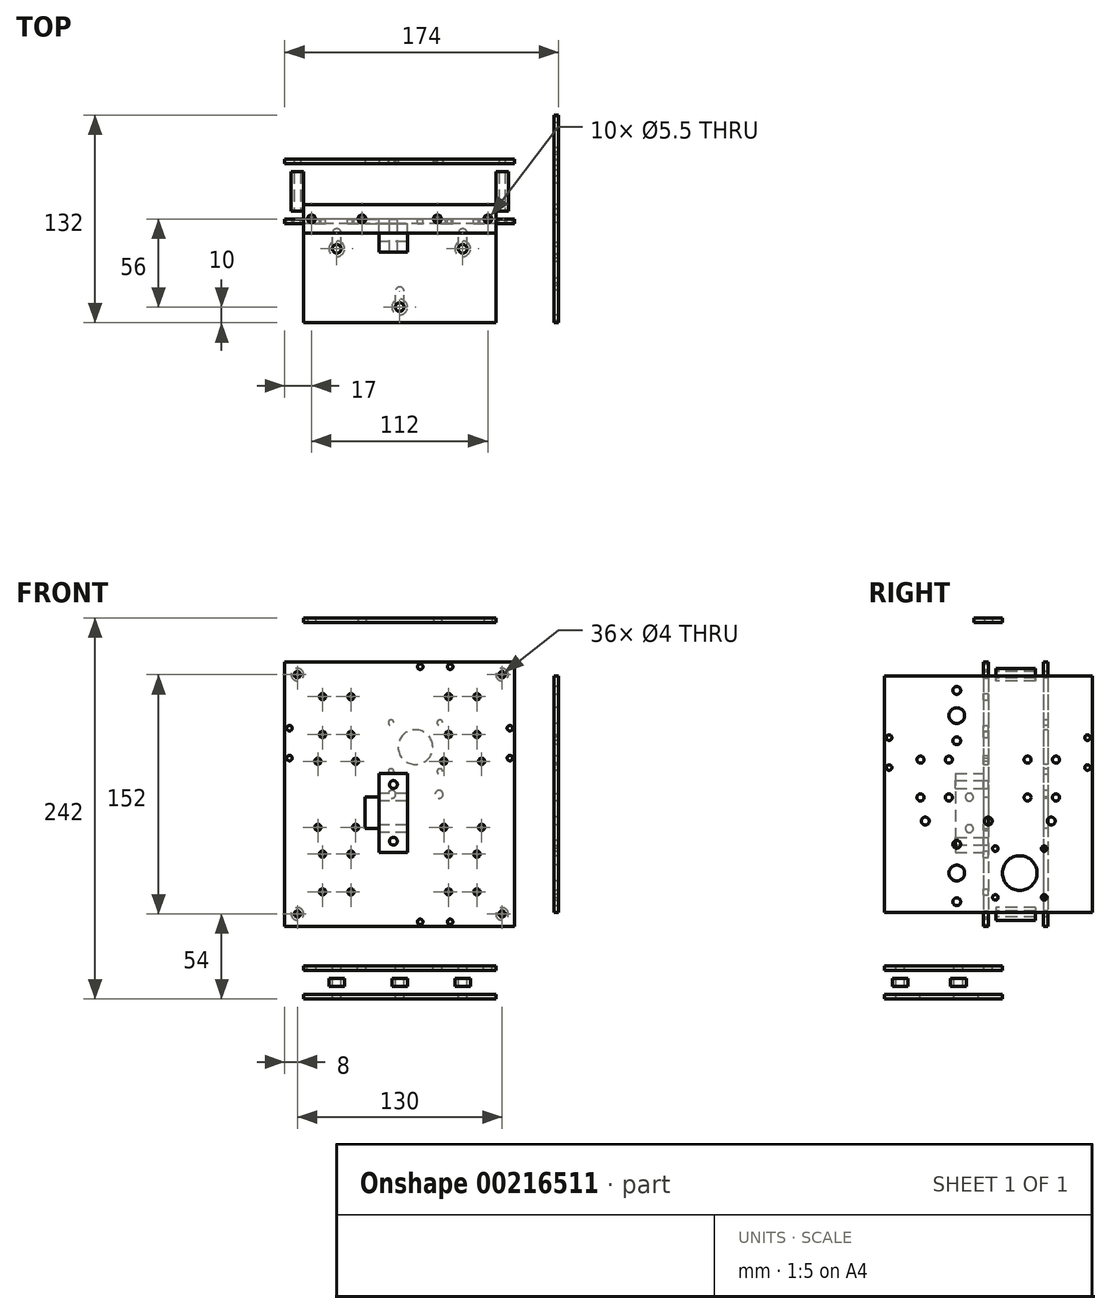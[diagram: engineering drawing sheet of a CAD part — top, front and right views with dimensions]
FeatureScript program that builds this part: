
annotation { "Feature Type Name" : "Feature", "Feature Type Description" : "" }
export const myFeature = defineFeature(function(context is Context, id is Id, definition is map)
    precondition{}
    {
        {
            assignVariable(context, id + "F0", {"name" : "Thickness", "anyValue" : 3});
        }
        {
            var Q0;
            Q0=qCreatedBy(makeId("Front.planeOp"),FACE);
            var sketch = newSketch(context, id + "F1", { "sketchPlane" : qUnion([Q0])});
            skLineSegment(sketch, "E0.bottom", {"start": v(73, 84) * mm, "end": v(-73, 84) * mm});
            skLineSegment(sketch, "E0.top", {"start": v(73, -84) * mm, "end": v(-73, -84) * mm});
            skLineSegment(sketch, "E0.left", {"start": v(73, 84) * mm, "end": v(73, -84) * mm});
            skLineSegment(sketch, "E0.right", {"start": v(-73, 84) * mm, "end": v(-73, -84) * mm});
            skPoint(sketch, "E0.middle", {"position": v(0, 0) * mm});
            skLineSegment(sketch, "E1", {"start": v(-49, -83.08) * mm, "end": v(-49, 79.73) * mm, "construction": true});
            skLineSegment(sketch, "E2", {"start": v(-31, -83.97) * mm, "end": v(-31, 79.73) * mm, "construction": true});
            skLineSegment(sketch, "E3", {"start": v(-55.64, 38) * mm, "end": v(56.55, 38) * mm, "construction": true});
            skLineSegment(sketch, "E4", {"start": v(-58.53, 62) * mm, "end": v(58.53, 62) * mm, "construction": true});
            skCircle(sketch, "E5", {"center": v(-49, 38) * mm, "radius": 2 * mm});
            skCircle(sketch, "E6", {"center": v(-49, 62) * mm, "radius": 2 * mm});
            skCircle(sketch, "E7", {"center": v(-31, 38) * mm, "radius": 2 * mm});
            skCircle(sketch, "E8", {"center": v(-31, 62) * mm, "radius": 2 * mm});
            skLineSegment(sketch, "E9", {"start": v(-72.74, 50) * mm, "end": v(58.97, 50) * mm, "construction": true});
            skLineSegment(sketch, "E10", {"start": v(-40, 79.29) * mm, "end": v(-40, -83.3) * mm, "construction": true});
            skLineSegment(sketch, "E11", {"start": v(-69.64, -50) * mm, "end": v(60.08, -50) * mm, "construction": true});
            skLineSegment(sketch, "E12", {"start": v(-58.61, -38) * mm, "end": v(58.75, -38) * mm, "construction": true});
            skLineSegment(sketch, "E13", {"start": v(-57.29, -62) * mm, "end": v(60.52, -62) * mm, "construction": true});
            skLineSegment(sketch, "E14", {"start": v(40, 79.29) * mm, "end": v(40, -84.85) * mm, "construction": true});
            skLineSegment(sketch, "E15", {"start": v(49, 79.07) * mm, "end": v(49, -84.4) * mm, "construction": true});
            skLineSegment(sketch, "E16", {"start": v(31, 79.29) * mm, "end": v(31, -83.74) * mm, "construction": true});
            skCircle(sketch, "E17", {"center": v(-49, -38) * mm, "radius": 2 * mm});
            skCircle(sketch, "E18", {"center": v(-31, -38) * mm, "radius": 2 * mm});
            skCircle(sketch, "E19", {"center": v(-49, -62) * mm, "radius": 2 * mm});
            skCircle(sketch, "E20", {"center": v(-31, -62) * mm, "radius": 2 * mm});
            skCircle(sketch, "E21", {"center": v(31, 62) * mm, "radius": 2 * mm});
            skCircle(sketch, "E22", {"center": v(49, 62) * mm, "radius": 2 * mm});
            skCircle(sketch, "E23", {"center": v(31, 38) * mm, "radius": 2 * mm});
            skCircle(sketch, "E24", {"center": v(49, 38) * mm, "radius": 2 * mm});
            skCircle(sketch, "E25", {"center": v(31, -38) * mm, "radius": 2 * mm});
            skCircle(sketch, "E26", {"center": v(49, -38) * mm, "radius": 2 * mm});
            skCircle(sketch, "E27", {"center": v(31, -62) * mm, "radius": 2 * mm});
            skCircle(sketch, "E28", {"center": v(49, -62) * mm, "radius": 2 * mm});
            skLineSegment(sketch, "E29", {"start": v(-70, 88.6) * mm, "end": v(-70, -88.82) * mm, "construction": true});
            skLineSegment(sketch, "E30", {"start": v(70, 90.06) * mm, "end": v(70, -91.23) * mm, "construction": true});
            skLineSegment(sketch, "E31", {"start": v(-72.75, 23) * mm, "end": v(68.8, 23) * mm, "construction": true});
            skCircle(sketch, "E32", {"center": v(-70, 23) * mm, "radius": 1.75 * mm});
            skCircle(sketch, "E33", {"center": v(70, 23) * mm, "radius": 1.75 * mm});
            skCircle(sketch, "E34", {"center": v(70, 42) * mm, "radius": 1.75 * mm});
            skCircle(sketch, "E35", {"center": v(-70, 42) * mm, "radius": 1.75 * mm});
            skLineSegment(sketch, "E36", {"start": v(-90.6, 21) * mm, "end": v(91.23, 21) * mm, "construction": true});
            skLineSegment(sketch, "E37", {"start": v(-89.18, -21) * mm, "end": v(89.82, -21) * mm, "construction": true});
            skLineSegment(sketch, "E38", {"start": v(28, 79.48) * mm, "end": v(28, -94.8) * mm, "construction": true});
            skLineSegment(sketch, "E39", {"start": v(52, 79.96) * mm, "end": v(52, -92.22) * mm, "construction": true});
            skLineSegment(sketch, "E40", {"start": v(-52, 80.9) * mm, "end": v(-52, -84.92) * mm, "construction": true});
            skLineSegment(sketch, "E41", {"start": v(-28, 79.72) * mm, "end": v(-28, -83.5) * mm, "construction": true});
            skCircle(sketch, "E42", {"center": v(-52, -21) * mm, "radius": 2 * mm});
            skCircle(sketch, "E43", {"center": v(-28, -21) * mm, "radius": 2 * mm});
            skCircle(sketch, "E44", {"center": v(-52, 21) * mm, "radius": 2 * mm});
            skCircle(sketch, "E45", {"center": v(-28, 21) * mm, "radius": 2 * mm});
            skCircle(sketch, "E46", {"center": v(28, 21) * mm, "radius": 2 * mm});
            skCircle(sketch, "E47", {"center": v(52, 21) * mm, "radius": 2 * mm});
            skCircle(sketch, "E48", {"center": v(52, -21) * mm, "radius": 2 * mm});
            skCircle(sketch, "E49", {"center": v(28, -21) * mm, "radius": 2 * mm});
            skLineSegment(sketch, "E50", {"start": v(-83.47, 81) * mm, "end": v(76.81, 81) * mm, "construction": true});
            skLineSegment(sketch, "E51", {"start": v(13, 80.28) * mm, "end": v(13, -83.41) * mm, "construction": true});
            skLineSegment(sketch, "E52", {"start": v(32, 79.81) * mm, "end": v(32, -83.41) * mm, "construction": true});
            skLineSegment(sketch, "E53", {"start": v(-76.56, -81) * mm, "end": v(71.61, -81) * mm, "construction": true});
            skCircle(sketch, "E54", {"center": v(13, -81) * mm, "radius": 1.75 * mm});
            skCircle(sketch, "E55", {"center": v(32, -81) * mm, "radius": 1.75 * mm});
            skCircle(sketch, "E56", {"center": v(13, 81) * mm, "radius": 1.75 * mm});
            skCircle(sketch, "E57", {"center": v(32, 81) * mm, "radius": 1.75 * mm});
            skCircle(sketch, "E58", {"center": v(-65, 76) * mm, "radius": 2 * mm});
            skCircle(sketch, "E59", {"center": v(65, 76) * mm, "radius": 2 * mm});
            skCircle(sketch, "E60", {"center": v(-65, -76) * mm, "radius": 2 * mm});
            skCircle(sketch, "E61", {"center": v(65, -76) * mm, "radius": 2 * mm});
            skLineSegment(sketch, "E62", {"start": v(-65, 88.6) * mm, "end": v(-65, -88.82) * mm, "construction": true});
            skLineSegment(sketch, "E63", {"start": v(65, 90.06) * mm, "end": v(65, -88.82) * mm, "construction": true});
            skLineSegment(sketch, "E64", {"start": v(-83.47, 76) * mm, "end": v(71.61, 76) * mm, "construction": true});
            skLineSegment(sketch, "E65", {"start": v(-76.56, -76) * mm, "end": v(71.61, -76) * mm, "construction": true});
            skLineSegment(sketch, "E66", {"start": v(-23, 79.72) * mm, "end": v(-23, -83.5) * mm, "construction": true});
            skLineSegment(sketch, "E67", {"start": v(-57, 81) * mm, "end": v(-57, -84.92) * mm, "construction": true});
            skLineSegment(sketch, "E68.bottom", {"start": v(-22, -1.8) * mm, "end": v(-13, -1.8) * mm});
            skLineSegment(sketch, "E68.top", {"start": v(-22, -21.8) * mm, "end": v(-13, -21.8) * mm});
            skLineSegment(sketch, "E68.left", {"start": v(-22, -1.8) * mm, "end": v(-22, -21.8) * mm});
            skLineSegment(sketch, "E68.right", {"start": v(-13, -1.8) * mm, "end": v(-13, -21.8) * mm});
            skLineSegment(sketch, "E69.bottom", {"start": v(-13, 13.2) * mm, "end": v(5, 13.2) * mm});
            skLineSegment(sketch, "E69.top", {"start": v(-13, -36.8) * mm, "end": v(5, -36.8) * mm});
            skLineSegment(sketch, "E69.left", {"start": v(-13, 13.2) * mm, "end": v(-13, -36.8) * mm});
            skLineSegment(sketch, "E69.right", {"start": v(5, 13.2) * mm, "end": v(5, -36.8) * mm});
            skLineSegment(sketch, "E70", {"start": v(-4, 17.89) * mm, "end": v(-4, -41.5) * mm, "construction": true});
            skCircle(sketch, "E71", {"center": v(-4, 6.2) * mm, "radius": 2.5 * mm});
            skCircle(sketch, "E72", {"center": v(-4, -29.8) * mm, "radius": 2.5 * mm});
            skLineSegment(sketch, "E73", {"start": v(-25.34, -11.8) * mm, "end": v(18.01, -11.8) * mm, "construction": true});
            skPoint(sketch, "E74", {"position": v(-4, 13.2) * mm});
            skPoint(sketch, "E75", {"position": v(-4, -11.8) * mm});
            skSolve(sketch);
        }
        {
            var Q0;
            Q0=makeQuery(id+"F1.imprint","IMPRINT",FACE,{"disambiguationData":[TD([[makeQuery(id+"F1.imprint","IMPRINT",EDGE,{"derivedFrom":sQuery(id+"F1.wireOp",EDGE,"E0.bottom")}),1.0]])]});
            var Q1;
            Q1=makeQuery(id+"F1.imprint","IMPRINT",FACE,{"disambiguationData":[TD([[makeQuery(id+"F1.imprint","IMPRINT",EDGE,{"derivedFrom":sQuery(id+"F1.wireOp",EDGE,"E69.bottom")}),-1.0]])]});
            extrude(context, id + "F2", {"entities" : qUnion([Q0, Q1]), "depth" : (getVariable(context, 'Thickness')) * mm});
        }
        {
            var Q0;
            Q0=makeQuery(id+"F1.imprint","IMPRINT",FACE,{"disambiguationData":[TD([[makeQuery(id+"F1.imprint","IMPRINT",EDGE,{"derivedFrom":sQuery(id+"F1.wireOp",EDGE,"E69.bottom")}),-1.0]])]});
            extrude(context, id + "F3", {"entities" : qUnion([Q0]), "depth" : 21 * mm, "hasSecondDirection" : true, "secondDirectionOppositeDirection" : false, "secondDirectionDepth" : 3 * mm});
        }
        {
            var Q0;
            Q0=makeQuery(id+"F3.opExtrude","SWEPT_FACE",FACE,{"disambiguationData":[OSD([sQuery(id+"F1.wireOp",EDGE,"E69.left")])]});
            var sketch = newSketch(context, id + "F4", { "sketchPlane" : qUnion([Q0])});
            skLineSegment(sketch, "E76", {"start": v(12, -1.15) * mm, "end": v(12, -40.85) * mm, "construction": true});
            skCircle(sketch, "E77", {"center": v(12, -1.8) * mm, "radius": 2.5 * mm});
            skCircle(sketch, "E78", {"center": v(12, -21.8) * mm, "radius": 2.5 * mm});
            skLineSegment(sketch, "E79", {"start": v(-1.92, -11.8) * mm, "end": v(22.84, -11.8) * mm, "construction": true});
            skCircle(sketch, "E80", {"center": v(12, -1.8) * mm, "radius": 9 * mm, "construction": true});
            skCircle(sketch, "E81", {"center": v(12, -21.8) * mm, "radius": 9 * mm, "construction": true});
            skSolve(sketch);
        }
        {
            var Q0;
            Q0=makeQuery(id+"F4.imprint","IMPRINT",FACE,{"disambiguationData":[TD([[makeQuery(id+"F4.imprint","IMPRINT",EDGE,{"derivedFrom":sQuery(id+"F4.wireOp",EDGE,"E77")}),1.0]])]});
            var Q1;
            Q1=makeQuery(id+"F4.imprint","IMPRINT",FACE,{"disambiguationData":[TD([[makeQuery(id+"F4.imprint","IMPRINT",EDGE,{"derivedFrom":sQuery(id+"F4.wireOp",EDGE,"E78")}),1.0]])]});
            extrude(context, id + "F5", {"entities" : qUnion([Q0, Q1]), "operationType" : NewBodyOperationType.REMOVE, "endBound" : BoundingType.THROUGH_ALL, "oppositeDirection" : true, "depth" : 25 * mm});
        }
        {
            var Q0;
            Q0=makeQuery(id+"F2.opExtrude","CAP_FACE",FACE,{"disambiguationData":[OSD([sQuery(id+"F1.wireOp",EDGE,"E0.bottom"),sQuery(id+"F1.wireOp",EDGE,"E0.top"),sQuery(id+"F1.wireOp",EDGE,"E0.left"),sQuery(id+"F1.wireOp",EDGE,"E0.right"),sQuery(id+"F1.wireOp",EDGE,"E5"),sQuery(id+"F1.wireOp",EDGE,"E6"),sQuery(id+"F1.wireOp",EDGE,"E7"),sQuery(id+"F1.wireOp",EDGE,"E8"),sQuery(id+"F1.wireOp",EDGE,"E17"),sQuery(id+"F1.wireOp",EDGE,"E18"),sQuery(id+"F1.wireOp",EDGE,"E19"),sQuery(id+"F1.wireOp",EDGE,"E20"),sQuery(id+"F1.wireOp",EDGE,"E21"),sQuery(id+"F1.wireOp",EDGE,"E22"),sQuery(id+"F1.wireOp",EDGE,"E23"),sQuery(id+"F1.wireOp",EDGE,"E24"),sQuery(id+"F1.wireOp",EDGE,"E25"),sQuery(id+"F1.wireOp",EDGE,"E26"),sQuery(id+"F1.wireOp",EDGE,"E27"),sQuery(id+"F1.wireOp",EDGE,"E28"),sQuery(id+"F1.wireOp",EDGE,"E32"),sQuery(id+"F1.wireOp",EDGE,"E33"),sQuery(id+"F1.wireOp",EDGE,"E34"),sQuery(id+"F1.wireOp",EDGE,"E35"),sQuery(id+"F1.wireOp",EDGE,"E42"),sQuery(id+"F1.wireOp",EDGE,"E43"),sQuery(id+"F1.wireOp",EDGE,"E44"),sQuery(id+"F1.wireOp",EDGE,"E45"),sQuery(id+"F1.wireOp",EDGE,"E46"),sQuery(id+"F1.wireOp",EDGE,"E47"),sQuery(id+"F1.wireOp",EDGE,"E48"),sQuery(id+"F1.wireOp",EDGE,"E49"),sQuery(id+"F1.wireOp",EDGE,"E54"),sQuery(id+"F1.wireOp",EDGE,"E55"),sQuery(id+"F1.wireOp",EDGE,"E56"),sQuery(id+"F1.wireOp",EDGE,"E57"),sQuery(id+"F1.wireOp",EDGE,"E58"),sQuery(id+"F1.wireOp",EDGE,"E59"),sQuery(id+"F1.wireOp",EDGE,"E60"),sQuery(id+"F1.wireOp",EDGE,"E61")])],"isStart":true});
            cPlane(context, id + "F6", {"entities" : qUnion([Q0]), "cplaneType" : CPlaneType.OFFSET, "offset" : 5 * mm, "width" : 150 * mm, "height" : 150 * mm});
        }
        {
            var Q0;
            Q0=qCreatedBy(id+"F6.planeOp",FACE);
            var sketch = newSketch(context, id + "F7", { "sketchPlane" : qUnion([Q0])});
            skCircle(sketch, "E82.0", {"center": v(65, 76) * mm, "radius": 2 * mm});
            skCircle(sketch, "E82.1", {"center": v(65, -76) * mm, "radius": 2 * mm});
            skCircle(sketch, "E82.2", {"center": v(-65, -76) * mm, "radius": 2 * mm});
            skCircle(sketch, "E82.3", {"center": v(-65, 76) * mm, "radius": 2 * mm});
            skCircle(sketch, "E83", {"center": v(65, 76) * mm, "radius": 4 * mm});
            skCircle(sketch, "E84", {"center": v(65, -76) * mm, "radius": 4 * mm});
            skCircle(sketch, "E85", {"center": v(-65, -76) * mm, "radius": 4 * mm});
            skCircle(sketch, "E86", {"center": v(-65, 76) * mm, "radius": 4 * mm});
            skSolve(sketch);
        }
        {
            var Q0;
            Q0=makeQuery(id+"F7.imprint","IMPRINT",FACE,{"disambiguationData":[TD([[makeQuery(id+"F7.imprint","IMPRINT",EDGE,{"derivedFrom":sQuery(id+"F7.wireOp",EDGE,"E82.0")}),-1.0]])]});
            var Q1;
            Q1=makeQuery(id+"F7.imprint","IMPRINT",FACE,{"disambiguationData":[TD([[makeQuery(id+"F7.imprint","IMPRINT",EDGE,{"derivedFrom":sQuery(id+"F7.wireOp",EDGE,"E82.1")}),-1.0]])]});
            var Q2;
            Q2=makeQuery(id+"F7.imprint","IMPRINT",FACE,{"disambiguationData":[TD([[makeQuery(id+"F7.imprint","IMPRINT",EDGE,{"derivedFrom":sQuery(id+"F7.wireOp",EDGE,"E82.2")}),-1.0]])]});
            var Q3;
            Q3=makeQuery(id+"F7.imprint","IMPRINT",FACE,{"disambiguationData":[TD([[makeQuery(id+"F7.imprint","IMPRINT",EDGE,{"derivedFrom":sQuery(id+"F7.wireOp",EDGE,"E82.3")}),-1.0]])]});
            extrude(context, id + "F8", {"entities" : qUnion([Q0, Q1, Q2, Q3]), "depth" : 25 * mm});
        }
        {
            var Q0;
            Q0=makeQuery(id+"F2.opExtrude","CAP_FACE",FACE,{"disambiguationData":[OSD([sQuery(id+"F1.wireOp",EDGE,"E0.bottom"),sQuery(id+"F1.wireOp",EDGE,"E0.top"),sQuery(id+"F1.wireOp",EDGE,"E0.left"),sQuery(id+"F1.wireOp",EDGE,"E0.right"),sQuery(id+"F1.wireOp",EDGE,"E5"),sQuery(id+"F1.wireOp",EDGE,"E6"),sQuery(id+"F1.wireOp",EDGE,"E7"),sQuery(id+"F1.wireOp",EDGE,"E8"),sQuery(id+"F1.wireOp",EDGE,"E17"),sQuery(id+"F1.wireOp",EDGE,"E18"),sQuery(id+"F1.wireOp",EDGE,"E19"),sQuery(id+"F1.wireOp",EDGE,"E20"),sQuery(id+"F1.wireOp",EDGE,"E21"),sQuery(id+"F1.wireOp",EDGE,"E22"),sQuery(id+"F1.wireOp",EDGE,"E23"),sQuery(id+"F1.wireOp",EDGE,"E24"),sQuery(id+"F1.wireOp",EDGE,"E25"),sQuery(id+"F1.wireOp",EDGE,"E26"),sQuery(id+"F1.wireOp",EDGE,"E27"),sQuery(id+"F1.wireOp",EDGE,"E28"),sQuery(id+"F1.wireOp",EDGE,"E32"),sQuery(id+"F1.wireOp",EDGE,"E33"),sQuery(id+"F1.wireOp",EDGE,"E34"),sQuery(id+"F1.wireOp",EDGE,"E35"),sQuery(id+"F1.wireOp",EDGE,"E42"),sQuery(id+"F1.wireOp",EDGE,"E43"),sQuery(id+"F1.wireOp",EDGE,"E44"),sQuery(id+"F1.wireOp",EDGE,"E45"),sQuery(id+"F1.wireOp",EDGE,"E46"),sQuery(id+"F1.wireOp",EDGE,"E47"),sQuery(id+"F1.wireOp",EDGE,"E48"),sQuery(id+"F1.wireOp",EDGE,"E49"),sQuery(id+"F1.wireOp",EDGE,"E54"),sQuery(id+"F1.wireOp",EDGE,"E55"),sQuery(id+"F1.wireOp",EDGE,"E56"),sQuery(id+"F1.wireOp",EDGE,"E57"),sQuery(id+"F1.wireOp",EDGE,"E58"),sQuery(id+"F1.wireOp",EDGE,"E59"),sQuery(id+"F1.wireOp",EDGE,"E60"),sQuery(id+"F1.wireOp",EDGE,"E61")])],"isStart":true});
            cPlane(context, id + "F9", {"entities" : qUnion([Q0]), "cplaneType" : CPlaneType.OFFSET, "offset" : 35 * mm, "width" : 150 * mm, "height" : 150 * mm});
        }
        {
            var Q0;
            Q0=qCreatedBy(id+"F9.planeOp",FACE);
            var sketch = newSketch(context, id + "F10", { "sketchPlane" : qUnion([Q0])});
            skLineSegment(sketch, "E87.0", {"start": v(-73, 84) * mm, "end": v(73, 84) * mm});
            skLineSegment(sketch, "E87.1", {"start": v(-73, 84) * mm, "end": v(-73, -84) * mm});
            skLineSegment(sketch, "E87.2", {"start": v(73, 84) * mm, "end": v(73, -84) * mm});
            skLineSegment(sketch, "E87.3", {"start": v(-73, -84) * mm, "end": v(73, -84) * mm});
            skLineSegment(sketch, "E87.4", {"start": v(22, -1.8) * mm, "end": v(22, -21.8) * mm});
            skLineSegment(sketch, "E87.5", {"start": v(13, -1.8) * mm, "end": v(13, -21.8) * mm});
            skLineSegment(sketch, "E87.6", {"start": v(22, -1.8) * mm, "end": v(13, -1.8) * mm});
            skLineSegment(sketch, "E87.7", {"start": v(22, -21.8) * mm, "end": v(13, -21.8) * mm});
            skLineSegment(sketch, "E88.bottom", {"start": v(-31, 51) * mm, "end": v(11, 51) * mm, "construction": true});
            skLineSegment(sketch, "E88.top", {"start": v(-31, 9) * mm, "end": v(11, 9) * mm, "construction": true});
            skLineSegment(sketch, "E88.left", {"start": v(-31, 51) * mm, "end": v(-31, 9) * mm, "construction": true});
            skLineSegment(sketch, "E88.right", {"start": v(11, 51) * mm, "end": v(11, 9) * mm, "construction": true});
            skLineSegment(sketch, "E89", {"start": v(-10, 94.34) * mm, "end": v(-10, -34.34) * mm, "construction": true});
            skLineSegment(sketch, "E90", {"start": v(-37.71, 30) * mm, "end": v(17.71, 30) * mm});
            skLineSegment(sketch, "E91.bottom", {"start": v(-25.5, 45.5) * mm, "end": v(5.5, 45.5) * mm, "construction": true});
            skLineSegment(sketch, "E91.top", {"start": v(-25.5, 14.5) * mm, "end": v(5.5, 14.5) * mm, "construction": true});
            skLineSegment(sketch, "E91.left", {"start": v(-25.5, 45.5) * mm, "end": v(-25.5, 14.5) * mm, "construction": true});
            skLineSegment(sketch, "E91.right", {"start": v(5.5, 45.5) * mm, "end": v(5.5, 14.5) * mm, "construction": true});
            skPoint(sketch, "E92", {"position": v(-10, 30) * mm});
            skCircle(sketch, "E93", {"center": v(-25.5, 45.5) * mm, "radius": 1.75 * mm});
            skCircle(sketch, "E94", {"center": v(5.5, 45.5) * mm, "radius": 1.75 * mm});
            skCircle(sketch, "E95", {"center": v(5.5, 14.5) * mm, "radius": 1.75 * mm});
            skCircle(sketch, "E96", {"center": v(-25.5, 14.5) * mm, "radius": 1.75 * mm});
            skCircle(sketch, "E97", {"center": v(-10, 30) * mm, "radius": 11 * mm});
            skLineSegment(sketch, "E98", {"start": v(-78.46, 0) * mm, "end": v(78.46, 0) * mm, "construction": true});
            skLineSegment(sketch, "E99", {"start": v(40, 94.7) * mm, "end": v(40, -94.7) * mm, "construction": true});
            skLineSegment(sketch, "E100", {"start": v(-40, 94.7) * mm, "end": v(-40, -94.7) * mm, "construction": true});
            skLineSegment(sketch, "E101", {"start": v(-79.3, -50) * mm, "end": v(80.19, -50) * mm, "construction": true});
            skLineSegment(sketch, "E102", {"start": v(80.19, 50) * mm, "end": v(-79.3, 50) * mm, "construction": true});
            skLineSegment(sketch, "E103", {"start": v(0, 94.7) * mm, "end": v(0, -94.7) * mm, "construction": true});
            skCircle(sketch, "E104.0", {"center": v(-65, 76) * mm, "radius": 2 * mm});
            skCircle(sketch, "E104.1", {"center": v(65, 76) * mm, "radius": 2 * mm});
            skCircle(sketch, "E104.2", {"center": v(65, -76) * mm, "radius": 2 * mm});
            skCircle(sketch, "E104.3", {"center": v(-65, -76) * mm, "radius": 2 * mm});
            skCircle(sketch, "E105", {"center": v(5, 0) * mm, "radius": 2.5 * mm});
            skCircle(sketch, "E106", {"center": v(-25, 0) * mm, "radius": 2.5 * mm});
            skCircle(sketch, "E107", {"center": v(-25, 0) * mm, "radius": 9 * mm, "construction": true});
            skCircle(sketch, "E108", {"center": v(5, 0) * mm, "radius": 9 * mm, "construction": true});
            skSolve(sketch);
        }
        {
            var Q0;
            Q0=makeQuery(id+"F10.imprint","IMPRINT",FACE,{"disambiguationData":[TD([[makeQuery(id+"F10.imprint","IMPRINT",EDGE,{"derivedFrom":sQuery(id+"F10.wireOp",EDGE,"E87.0")}),-1.0]])]});
            extrude(context, id + "F11", {"entities" : qUnion([Q0]), "depth" : (getVariable(context, 'Thickness')) * mm});
        }
        {
            var Q0;
            Q0=makeQuery(id+"F2.opExtrude","SWEPT_FACE",FACE,{"disambiguationData":[OSD([sQuery(id+"F1.wireOp",EDGE,"E0.bottom")])]});
            cPlane(context, id + "F12", {"entities" : qUnion([Q0]), "cplaneType" : CPlaneType.OFFSET, "offset" : 25 * mm, "width" : 150 * mm, "height" : 150 * mm});
        }
        {
            var Q0;
            Q0=qCreatedBy(id+"F12.planeOp",FACE);
            var sketch = newSketch(context, id + "F13", { "sketchPlane" : qUnion([Q0])});
            skLineSegment(sketch, "E109.bottom", {"start": v(61, -9) * mm, "end": v(-61, -9) * mm});
            skLineSegment(sketch, "E109.top", {"start": v(61, 9) * mm, "end": v(-61, 9) * mm});
            skLineSegment(sketch, "E109.left", {"start": v(61, -9) * mm, "end": v(61, 9) * mm});
            skLineSegment(sketch, "E109.right", {"start": v(-61, -9) * mm, "end": v(-61, 9) * mm});
            skPoint(sketch, "E109.middle", {"position": v(0, 0) * mm});
            skLineSegment(sketch, "E110", {"start": v(-40, -14.58) * mm, "end": v(-40, 18.52) * mm, "construction": true});
            skLineSegment(sketch, "E111", {"start": v(40, -14.81) * mm, "end": v(40, 21.3) * mm, "construction": true});
            skCircle(sketch, "E112", {"center": v(-56, 0) * mm, "radius": 2.5 * mm});
            skCircle(sketch, "E113", {"center": v(-24, 0) * mm, "radius": 2.5 * mm});
            skCircle(sketch, "E114", {"center": v(24, 0) * mm, "radius": 2.5 * mm});
            skCircle(sketch, "E115", {"center": v(56, 0) * mm, "radius": 2.5 * mm});
            skSolve(sketch);
        }
        {
            var Q0;
            Q0=makeQuery(id+"F13.imprint","IMPRINT",FACE,{"disambiguationData":[TD([[makeQuery(id+"F13.imprint","IMPRINT",EDGE,{"derivedFrom":sQuery(id+"F13.wireOp",EDGE,"E109.bottom")}),-1.0]])]});
            extrude(context, id + "F14", {"entities" : qUnion([Q0]), "depth" : (getVariable(context, 'Thickness')) * mm});
        }
        {
            var Q0;
            Q0=makeQuery(id+"F2.opExtrude","SWEPT_FACE",FACE,{"disambiguationData":[OSD([sQuery(id+"F1.wireOp",EDGE,"E0.top")])]});
            cPlane(context, id + "F15", {"entities" : qUnion([Q0]), "cplaneType" : CPlaneType.OFFSET, "offset" : 25 * mm, "width" : 150 * mm, "height" : 150 * mm});
        }
        {
            var Q0;
            Q0=qCreatedBy(id+"F15.planeOp",FACE);
            var sketch = newSketch(context, id + "F16", { "sketchPlane" : qUnion([Q0])});
            skLineSegment(sketch, "E116.bottom", {"start": v(61, -9) * mm, "end": v(-61, -9) * mm});
            skLineSegment(sketch, "E116.top", {"start": v(61, 66) * mm, "end": v(-61, 66) * mm});
            skLineSegment(sketch, "E116.left", {"start": v(61, -9) * mm, "end": v(61, 66) * mm});
            skLineSegment(sketch, "E116.right", {"start": v(-61, -9) * mm, "end": v(-61, 66) * mm});
            skPoint(sketch, "E116.middle", {"position": v(0, 28.5) * mm});
            skLineSegment(sketch, "E117", {"start": v(-62.7, 0) * mm, "end": v(63.63, 0) * mm, "construction": true});
            skCircle(sketch, "E118", {"center": v(-56, 0) * mm, "radius": 2.75 * mm});
            skCircle(sketch, "E119", {"center": v(-24, 0) * mm, "radius": 2.75 * mm});
            skCircle(sketch, "E120", {"center": v(24, 0) * mm, "radius": 2.75 * mm});
            skCircle(sketch, "E121", {"center": v(56, 0) * mm, "radius": 2.75 * mm});
            skLineSegment(sketch, "E122", {"start": v(60.53, 0) * mm, "end": v(-64.46, 0) * mm, "construction": true});
            skLineSegment(sketch, "E123", {"start": v(0, -36.2) * mm, "end": v(0, 36.61) * mm, "construction": true});
            skLineSegment(sketch, "E124", {"start": v(40, -36.2) * mm, "end": v(40, 36.61) * mm, "construction": true});
            skLineSegment(sketch, "E125", {"start": v(-40, -36.2) * mm, "end": v(-40, 36.61) * mm, "construction": true});
            skLineSegment(sketch, "E126", {"start": v(-62.32, 56) * mm, "end": v(63.27, 56) * mm, "construction": true});
            skLineSegment(sketch, "E127", {"start": v(-62.95, 19) * mm, "end": v(63.27, 19) * mm, "construction": true});
            skCircle(sketch, "E128", {"center": v(0, 56) * mm, "radius": 2.75 * mm});
            skCircle(sketch, "E129", {"center": v(-40, 19) * mm, "radius": 2.75 * mm});
            skCircle(sketch, "E130", {"center": v(40, 19) * mm, "radius": 2.75 * mm});
            skSolve(sketch);
        }
        {
            var Q0;
            Q0=makeQuery(id+"F16.imprint","IMPRINT",FACE,{"disambiguationData":[TD([[makeQuery(id+"F16.imprint","IMPRINT",EDGE,{"derivedFrom":sQuery(id+"F16.wireOp",EDGE,"E116.bottom")}),-1.0]])]});
            extrude(context, id + "F17", {"entities" : qUnion([Q0]), "depth" : (getVariable(context, 'Thickness')) * mm});
        }
        {
            var Q0;
            Q0=makeQuery(id+"F17.opExtrude","CAP_FACE",FACE,{"disambiguationData":[OSD([sQuery(id+"F16.wireOp",EDGE,"E116.bottom"),sQuery(id+"F16.wireOp",EDGE,"E116.top"),sQuery(id+"F16.wireOp",EDGE,"E116.left"),sQuery(id+"F16.wireOp",EDGE,"E116.right"),sQuery(id+"F16.wireOp",EDGE,"E118"),sQuery(id+"F16.wireOp",EDGE,"E119"),sQuery(id+"F16.wireOp",EDGE,"E120"),sQuery(id+"F16.wireOp",EDGE,"E121")])],"isStart":false});
            cPlane(context, id + "F18", {"entities" : qUnion([Q0]), "cplaneType" : CPlaneType.OFFSET, "offset" : 5 * mm, "width" : 150 * mm, "height" : 150 * mm});
        }
        {
            var Q0;
            Q0=qCreatedBy(id+"F18.planeOp",FACE);
            var sketch = newSketch(context, id + "F19", { "sketchPlane" : qUnion([Q0])});
            skCircle(sketch, "E131", {"center": v(0, 56) * mm, "radius": 5 * mm});
            skCircle(sketch, "E132", {"center": v(-40, 19) * mm, "radius": 5 * mm});
            skCircle(sketch, "E133", {"center": v(40, 19) * mm, "radius": 5 * mm});
            skCircle(sketch, "E134.0", {"center": v(-40, 19) * mm, "radius": 2.75 * mm});
            skCircle(sketch, "E135.0", {"center": v(0, 56) * mm, "radius": 2.75 * mm});
            skCircle(sketch, "E136.0", {"center": v(40, 19) * mm, "radius": 2.75 * mm});
            skSolve(sketch);
        }
        {
            var Q0;
            Q0=makeQuery(id+"F19.imprint","IMPRINT",FACE,{"disambiguationData":[TD([[makeQuery(id+"F19.imprint","IMPRINT",EDGE,{"derivedFrom":sQuery(id+"F19.wireOp",EDGE,"E132")}),1.0]])]});
            var Q1;
            Q1=makeQuery(id+"F19.imprint","IMPRINT",FACE,{"disambiguationData":[TD([[makeQuery(id+"F19.imprint","IMPRINT",EDGE,{"derivedFrom":sQuery(id+"F19.wireOp",EDGE,"E131")}),1.0]])]});
            var Q2;
            Q2=makeQuery(id+"F19.imprint","IMPRINT",FACE,{"disambiguationData":[TD([[makeQuery(id+"F19.imprint","IMPRINT",EDGE,{"derivedFrom":sQuery(id+"F19.wireOp",EDGE,"E133")}),1.0]])]});
            extrude(context, id + "F20", {"entities" : qUnion([Q0, Q1, Q2]), "depth" : 5 * mm});
        }
        {
            var Q0;
            Q0=makeQuery(id+"F17.opExtrude","CAP_FACE",FACE,{"disambiguationData":[OSD([sQuery(id+"F16.wireOp",EDGE,"E116.bottom"),sQuery(id+"F16.wireOp",EDGE,"E116.top"),sQuery(id+"F16.wireOp",EDGE,"E116.left"),sQuery(id+"F16.wireOp",EDGE,"E116.right"),sQuery(id+"F16.wireOp",EDGE,"E118"),sQuery(id+"F16.wireOp",EDGE,"E119"),sQuery(id+"F16.wireOp",EDGE,"E120"),sQuery(id+"F16.wireOp",EDGE,"E121"),sQuery(id+"F16.wireOp",EDGE,"E128"),sQuery(id+"F16.wireOp",EDGE,"E129"),sQuery(id+"F16.wireOp",EDGE,"E130")])],"isStart":false});
            cPlane(context, id + "F21", {"entities" : qUnion([Q0]), "cplaneType" : CPlaneType.OFFSET, "offset" : 15 * mm, "width" : 150 * mm, "height" : 150 * mm});
        }
        {
            var Q0;
            Q0=qCreatedBy(id+"F21.planeOp",FACE);
            var sketch = newSketch(context, id + "F22", { "sketchPlane" : qUnion([Q0])});
            skCircle(sketch, "E137.0", {"center": v(-40, 19) * mm, "radius": 2.75 * mm});
            skCircle(sketch, "E138.0", {"center": v(0, 56) * mm, "radius": 2.75 * mm});
            skCircle(sketch, "E139.0", {"center": v(40, 19) * mm, "radius": 2.75 * mm});
            skLineSegment(sketch, "E140.0", {"start": v(-61, -9) * mm, "end": v(-61, 66) * mm});
            skLineSegment(sketch, "E140.1", {"start": v(61, -9) * mm, "end": v(-61, -9) * mm});
            skLineSegment(sketch, "E140.2", {"start": v(61, -9) * mm, "end": v(61, 66) * mm});
            skLineSegment(sketch, "E140.3", {"start": v(61, 66) * mm, "end": v(-61, 66) * mm});
            skLineSegment(sketch, "E141", {"start": v(0, 56) * mm, "end": v(0, 46) * mm});
            skLineSegment(sketch, "E142", {"start": v(-40, 19) * mm, "end": v(-40, 9) * mm});
            skLineSegment(sketch, "E143", {"start": v(40, 19) * mm, "end": v(40, 9) * mm});
            skArc(sketch, "E144.0.startCap", {"start": v(-42.75, 19) * mm, "mid": v(-40, 21.75) * mm, "end": v(-37.25, 19) * mm});
            skArc(sketch, "E144.0.endCap", {"start": v(-37.25, 9) * mm, "mid": v(-40, 6.25) * mm, "end": v(-42.75, 9) * mm});
            skLineSegment(sketch, "E144.0.left", {"start": v(-37.25, 19) * mm, "end": v(-37.25, 9) * mm});
            skLineSegment(sketch, "E144.0.right", {"start": v(-42.75, 19) * mm, "end": v(-42.75, 9) * mm});
            skArc(sketch, "E144.1.startCap", {"start": v(-2.75, 56) * mm, "mid": v(0, 58.75) * mm, "end": v(2.75, 56) * mm});
            skArc(sketch, "E144.1.endCap", {"start": v(2.75, 46) * mm, "mid": v(0, 43.25) * mm, "end": v(-2.75, 46) * mm});
            skLineSegment(sketch, "E144.1.left", {"start": v(2.75, 56) * mm, "end": v(2.75, 46) * mm});
            skLineSegment(sketch, "E144.1.right", {"start": v(-2.75, 56) * mm, "end": v(-2.75, 46) * mm});
            skArc(sketch, "E144.2.startCap", {"start": v(37.25, 19) * mm, "mid": v(40, 21.75) * mm, "end": v(42.75, 19) * mm});
            skArc(sketch, "E144.2.endCap", {"start": v(42.75, 9) * mm, "mid": v(40, 6.25) * mm, "end": v(37.25, 9) * mm});
            skLineSegment(sketch, "E144.2.left", {"start": v(42.75, 19) * mm, "end": v(42.75, 9) * mm});
            skLineSegment(sketch, "E144.2.right", {"start": v(37.25, 19) * mm, "end": v(37.25, 9) * mm});
            skSolve(sketch);
        }
        {
            var Q0;
            Q0=qSketchRegion(id+"F22",true);
            extrude(context, id + "F23", {"entities" : qUnion([Q0]), "depth" : (getVariable(context, 'Thickness')) * mm});
        }
        {
            var Q0;
            Q0=makeQuery(id+"F2.opExtrude","SWEPT_FACE",FACE,{"disambiguationData":[OSD([sQuery(id+"F1.wireOp",EDGE,"E0.left")])]});
            cPlane(context, id + "F24", {"entities" : qUnion([Q0]), "cplaneType" : CPlaneType.OFFSET, "offset" : 25 * mm, "width" : 150 * mm, "height" : 150 * mm});
        }
        {
            var Q0;
            Q0=qCreatedBy(id+"F24.planeOp",FACE);
            var sketch = newSketch(context, id + "F25", { "sketchPlane" : qUnion([Q0])});
            skLineSegment(sketch, "E145.bottom", {"start": v(-66, 75) * mm, "end": v(66, 75) * mm});
            skLineSegment(sketch, "E145.top", {"start": v(-66, -75) * mm, "end": v(66, -75) * mm});
            skLineSegment(sketch, "E145.left", {"start": v(-66, 75) * mm, "end": v(-66, -75) * mm});
            skLineSegment(sketch, "E145.right", {"start": v(66, 75) * mm, "end": v(66, -75) * mm});
            skPoint(sketch, "E146", {"position": v(0, 0) * mm});
            skLineSegment(sketch, "E147", {"start": v(-126.8, 0) * mm, "end": v(119.29, 0) * mm, "construction": true});
            skLineSegment(sketch, "E148", {"start": v(0, 95.8) * mm, "end": v(0, -127.28) * mm, "construction": true});
            skLineSegment(sketch, "E149", {"start": v(-20, 95.8) * mm, "end": v(-20, -127.28) * mm, "construction": true});
            skLineSegment(sketch, "E150", {"start": v(-126.8, 50) * mm, "end": v(119.29, 50) * mm, "construction": true});
            skLineSegment(sketch, "E151", {"start": v(-126.8, -50) * mm, "end": v(119.29, -50) * mm, "construction": true});
            skCircle(sketch, "E152", {"center": v(-20, 50) * mm, "radius": 5 * mm});
            skCircle(sketch, "E153", {"center": v(-20, -50) * mm, "radius": 5 * mm});
            skLineSegment(sketch, "E154", {"start": v(-40, 95.8) * mm, "end": v(-40, -127.28) * mm, "construction": true});
            skLineSegment(sketch, "E155", {"start": v(20, 95.8) * mm, "end": v(20, -127.28) * mm, "construction": true});
            skLineSegment(sketch, "E156", {"start": v(40, -127.28) * mm, "end": v(40, 95.8) * mm, "construction": true});
            skCircle(sketch, "E157", {"center": v(20, -50) * mm, "radius": 11 * mm});
            skLineSegment(sketch, "E158.bottom", {"start": v(41, -71) * mm, "end": v(-1, -71) * mm, "construction": true});
            skLineSegment(sketch, "E158.top", {"start": v(41, -29) * mm, "end": v(-1, -29) * mm, "construction": true});
            skLineSegment(sketch, "E158.left", {"start": v(41, -71) * mm, "end": v(41, -29) * mm, "construction": true});
            skLineSegment(sketch, "E158.right", {"start": v(-1, -71) * mm, "end": v(-1, -29) * mm, "construction": true});
            skLineSegment(sketch, "E159.bottom", {"start": v(35.5, -65.5) * mm, "end": v(4.5, -65.5) * mm, "construction": true});
            skLineSegment(sketch, "E159.top", {"start": v(35.5, -34.5) * mm, "end": v(4.5, -34.5) * mm, "construction": true});
            skLineSegment(sketch, "E159.left", {"start": v(35.5, -65.5) * mm, "end": v(35.5, -34.5) * mm, "construction": true});
            skLineSegment(sketch, "E159.right", {"start": v(4.5, -65.5) * mm, "end": v(4.5, -34.5) * mm, "construction": true});
            skCircle(sketch, "E160", {"center": v(4.5, -34.5) * mm, "radius": 1.75 * mm});
            skCircle(sketch, "E161", {"center": v(35.5, -34.5) * mm, "radius": 1.75 * mm});
            skCircle(sketch, "E162", {"center": v(4.5, -65.5) * mm, "radius": 1.75 * mm});
            skCircle(sketch, "E163", {"center": v(35.5, -65.5) * mm, "radius": 1.75 * mm});
            skCircle(sketch, "E164", {"center": v(-20, -31.75) * mm, "radius": 2.5 * mm});
            skCircle(sketch, "E165", {"center": v(-20, -68.25) * mm, "radius": 2.5 * mm});
            skLineSegment(sketch, "E166", {"start": v(-126.8, -17) * mm, "end": v(119.29, -17) * mm, "construction": true});
            skCircle(sketch, "E167", {"center": v(-40, -17) * mm, "radius": 2.5 * mm});
            skCircle(sketch, "E168", {"center": v(0, -17) * mm, "radius": 2.5 * mm});
            skCircle(sketch, "E169", {"center": v(40, -17) * mm, "radius": 2.5 * mm});
            skCircle(sketch, "E170", {"center": v(-20, 66) * mm, "radius": 2.5 * mm});
            skCircle(sketch, "E171", {"center": v(-20, 34) * mm, "radius": 2.5 * mm});
            skLineSegment(sketch, "E172", {"start": v(-63, 95.8) * mm, "end": v(-63, -127.28) * mm, "construction": true});
            skLineSegment(sketch, "E173", {"start": v(63, 95.8) * mm, "end": v(63, -127.28) * mm, "construction": true});
            skLineSegment(sketch, "E174", {"start": v(-126.8, 10) * mm, "end": v(119.29, 10) * mm, "construction": true});
            skLineSegment(sketch, "E175", {"start": v(-34, 95.8) * mm, "end": v(-34, -127.28) * mm, "construction": true});
            skLineSegment(sketch, "E176", {"start": v(34, 95.8) * mm, "end": v(34, -127.28) * mm, "construction": true});
            skLineSegment(sketch, "E177.bottom", {"start": v(-25, -2) * mm, "end": v(-43, -2) * mm, "construction": true});
            skLineSegment(sketch, "E177.top", {"start": v(-25, 22) * mm, "end": v(-43, 22) * mm, "construction": true});
            skLineSegment(sketch, "E177.left", {"start": v(-25, -2) * mm, "end": v(-25, 22) * mm, "construction": true});
            skLineSegment(sketch, "E177.right", {"start": v(-43, -2) * mm, "end": v(-43, 22) * mm, "construction": true});
            skPoint(sketch, "E177.middle", {"position": v(-34, 10) * mm});
            skLineSegment(sketch, "E178.bottom", {"start": v(43, -2) * mm, "end": v(25, -2) * mm, "construction": true});
            skLineSegment(sketch, "E178.top", {"start": v(43, 22) * mm, "end": v(25, 22) * mm, "construction": true});
            skLineSegment(sketch, "E178.left", {"start": v(43, -2) * mm, "end": v(43, 22) * mm, "construction": true});
            skLineSegment(sketch, "E178.right", {"start": v(25, -2) * mm, "end": v(25, 22) * mm, "construction": true});
            skPoint(sketch, "E178.middle", {"position": v(34, 10) * mm});
            skCircle(sketch, "E179", {"center": v(-43, 22) * mm, "radius": 2.25 * mm});
            skCircle(sketch, "E180", {"center": v(-25, 22) * mm, "radius": 2.25 * mm});
            skCircle(sketch, "E181", {"center": v(-25, -2) * mm, "radius": 2.25 * mm});
            skCircle(sketch, "E182", {"center": v(-43, -2) * mm, "radius": 2.25 * mm});
            skCircle(sketch, "E183", {"center": v(25, 22) * mm, "radius": 2.25 * mm});
            skCircle(sketch, "E184", {"center": v(43, 22) * mm, "radius": 2.25 * mm});
            skCircle(sketch, "E185", {"center": v(25, -2) * mm, "radius": 2.25 * mm});
            skCircle(sketch, "E186", {"center": v(43, -2) * mm, "radius": 2.25 * mm});
            skCircle(sketch, "E187", {"center": v(-63, 36) * mm, "radius": 1.75 * mm});
            skCircle(sketch, "E188", {"center": v(-63, 17) * mm, "radius": 1.75 * mm});
            skCircle(sketch, "E189", {"center": v(63, 36) * mm, "radius": 1.75 * mm});
            skCircle(sketch, "E190", {"center": v(63, 17) * mm, "radius": 1.75 * mm});
            skSolve(sketch);
        }
        {
            var Q0;
            Q0=makeQuery(id+"F25.imprint","IMPRINT",FACE,{"disambiguationData":[TD([[makeQuery(id+"F25.imprint","IMPRINT",EDGE,{"derivedFrom":sQuery(id+"F25.wireOp",EDGE,"E145.bottom")}),-1.0]])]});
            extrude(context, id + "F26", {"entities" : qUnion([Q0]), "depth" : (getVariable(context, 'Thickness')) * mm});
        }
    });
